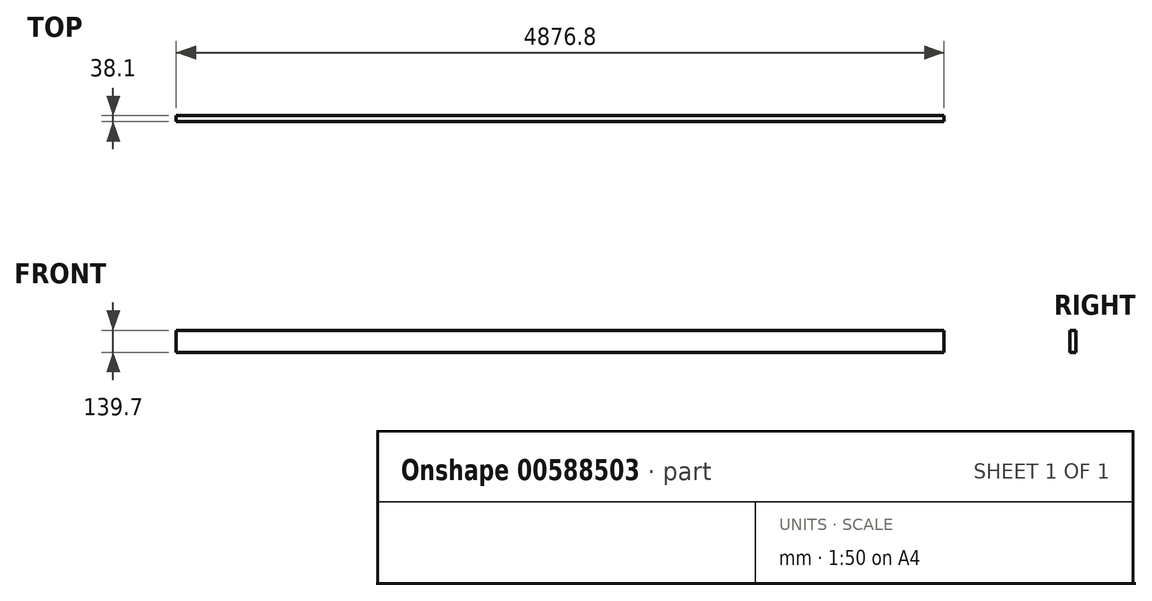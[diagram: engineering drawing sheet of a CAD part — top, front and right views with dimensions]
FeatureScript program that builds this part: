
annotation { "Feature Type Name" : "Feature", "Feature Type Description" : "" }
export const myFeature = defineFeature(function(context is Context, id is Id, definition is map)
    precondition{}
    {
        {
            var Q0;
            Q0=qCreatedBy(makeId("Right.planeOp"),FACE);
            var sketch = newSketch(context, id + "F0", { "sketchPlane" : qUnion([Q0])});
            skLineSegment(sketch, "E0.bottom", {"start": v(-65.02, 74.42) * mm, "end": v(-26.92, 74.42) * mm});
            skLineSegment(sketch, "E0.top", {"start": v(-65.02, -65.28) * mm, "end": v(-26.92, -65.28) * mm});
            skLineSegment(sketch, "E0.left", {"start": v(-65.02, 74.42) * mm, "end": v(-65.02, -65.28) * mm});
            skLineSegment(sketch, "E0.right", {"start": v(-26.92, 74.42) * mm, "end": v(-26.92, -65.28) * mm});
            skSolve(sketch);
        }
        {
            var Q0;
            Q0=makeQuery(id+"F0.imprint","IMPRINT",FACE,{"disambiguationData":[TD([[makeQuery(id+"F0.imprint","IMPRINT",EDGE,{"derivedFrom":sQuery(id+"F0.wireOp",EDGE,"E0.bottom")}),-1.0]])]});
            extrude(context, id + "F1", {"entities" : qUnion([Q0]), "depth" : 4876.8 * mm, "offsetDistance" : 25.4 * mm});
        }
    });
